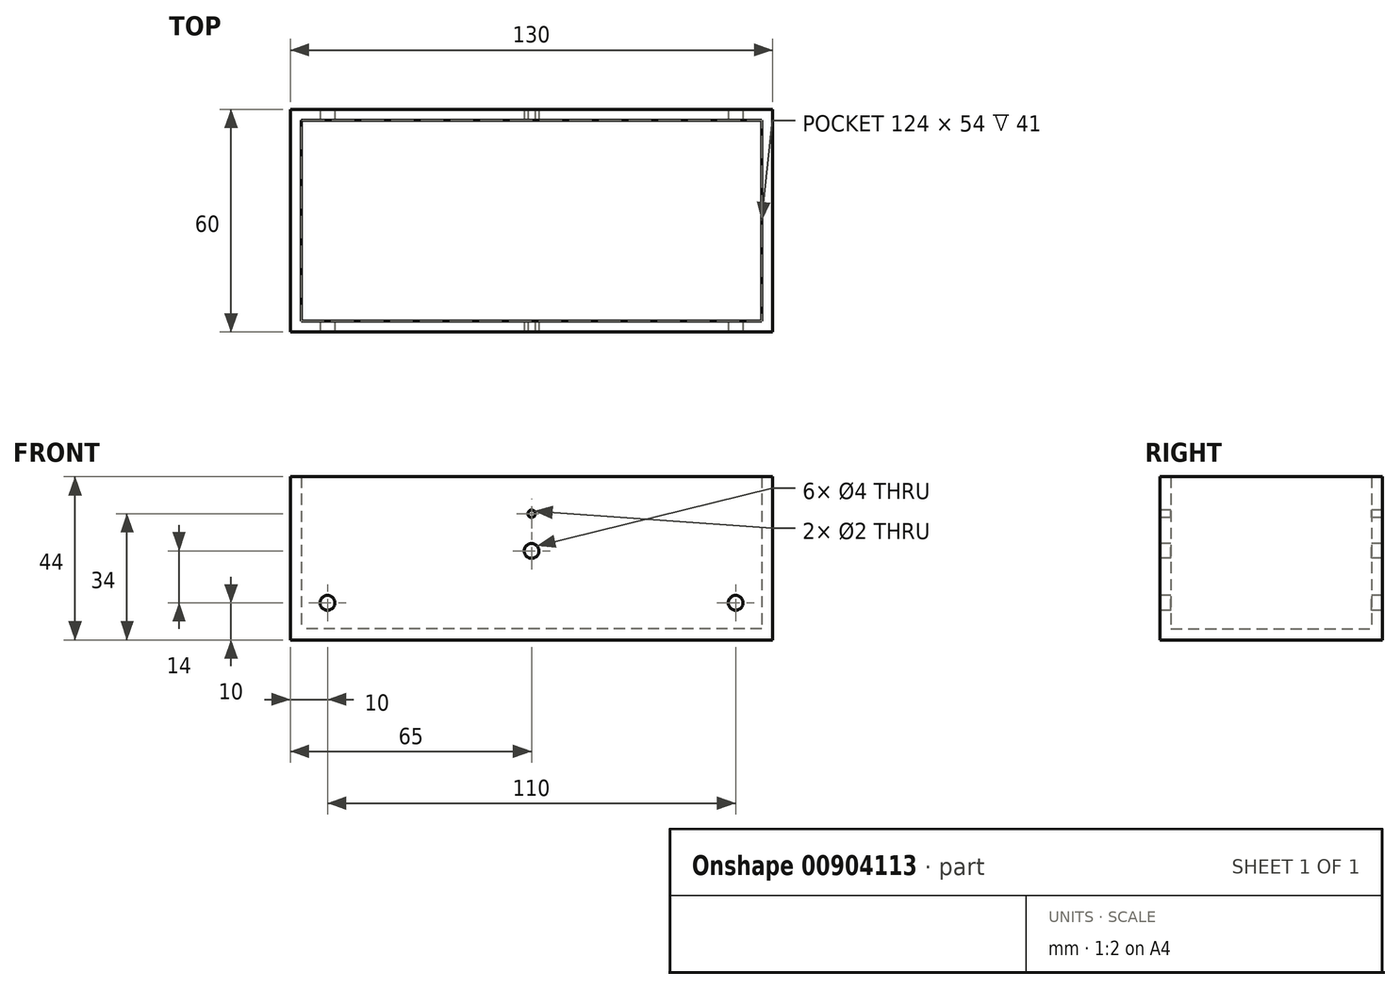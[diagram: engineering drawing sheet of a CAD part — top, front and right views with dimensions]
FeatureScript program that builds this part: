
annotation { "Feature Type Name" : "Feature", "Feature Type Description" : "" }
export const myFeature = defineFeature(function(context is Context, id is Id, definition is map)
    precondition{}
    {
        {
            var Q0;
            Q0=qCreatedBy(makeId("Top.planeOp"),FACE);
            var sketch = newSketch(context, id + "F0", { "sketchPlane" : qUnion([Q0])});
            skLineSegment(sketch, "E0.bottom", {"start": v(65, 30) * mm, "end": v(-65, 30) * mm});
            skLineSegment(sketch, "E0.top", {"start": v(65, -30) * mm, "end": v(-65, -30) * mm});
            skLineSegment(sketch, "E0.left", {"start": v(65, 30) * mm, "end": v(65, -30) * mm});
            skLineSegment(sketch, "E0.right", {"start": v(-65, 30) * mm, "end": v(-65, -30) * mm});
            skPoint(sketch, "E0.middle", {"position": v(0, 0) * mm});
            skLineSegment(sketch, "E1.0", {"start": v(62, 27) * mm, "end": v(-62, 27) * mm});
            skLineSegment(sketch, "E2.0", {"start": v(62, 27) * mm, "end": v(62, -27) * mm});
            skLineSegment(sketch, "E3.0", {"start": v(62, -27) * mm, "end": v(-62, -27) * mm});
            skLineSegment(sketch, "E4.0", {"start": v(-62, 27) * mm, "end": v(-62, -27) * mm});
            skSolve(sketch);
        }
        {
            var Q0;
            Q0 = qSketchRegion(id + "F0", true);
            extrude(context, id + "F1", {"entities" : qUnion([Q0]), "depth" : 44 * mm, "offsetDistance" : 25 * mm});
        }
        {
            var Q0;
            Q0=makeQuery(id+"F1.opExtrude","SWEPT_FACE",FACE,{"disambiguationData":[OSD([sQuery(id+"F0.wireOp",EDGE,"E0.top")])]});
            var sketch = newSketch(context, id + "F2", { "sketchPlane" : qUnion([Q0])});
            skCircle(sketch, "E5", {"center": v(55, 10) * mm, "radius": 2 * mm});
            skCircle(sketch, "E6", {"center": v(-55, 10) * mm, "radius": 2 * mm});
            skCircle(sketch, "E7", {"center": v(0, 24) * mm, "radius": 2 * mm});
            skCircle(sketch, "E8", {"center": v(0, 34) * mm, "radius": 1 * mm});
            skSolve(sketch);
        }
        {
            var Q0;
            Q0 = qSketchRegion(id + "F2", true);
            extrude(context, id + "F3", {"entities" : qUnion([Q0]), "operationType" : NewBodyOperationType.REMOVE, "endBound" : BoundingType.THROUGH_ALL, "oppositeDirection" : true, "depth" : 25 * mm, "offsetDistance" : 25 * mm});
        }
        {
            var Q0;
            Q0=qCreatedBy(makeId("Top.planeOp"),FACE);
            var sketch = newSketch(context, id + "F4", { "sketchPlane" : qUnion([Q0])});
            skLineSegment(sketch, "E9.bottom", {"start": v(62, -27) * mm, "end": v(-62, -27) * mm});
            skLineSegment(sketch, "E9.top", {"start": v(62, 27) * mm, "end": v(-62, 27) * mm});
            skLineSegment(sketch, "E9.left", {"start": v(62, -27) * mm, "end": v(62, 27) * mm});
            skLineSegment(sketch, "E9.right", {"start": v(-62, -27) * mm, "end": v(-62, 27) * mm});
            skPoint(sketch, "E9.middle", {"position": v(0, 0) * mm});
            skSolve(sketch);
        }
        {
            var Q0;
            Q0 = qSketchRegion(id + "F4", true);
            extrude(context, id + "F5", {"entities" : qUnion([Q0]), "operationType" : NewBodyOperationType.ADD, "depth" : 3 * mm, "offsetDistance" : 25 * mm});
        }
    });
